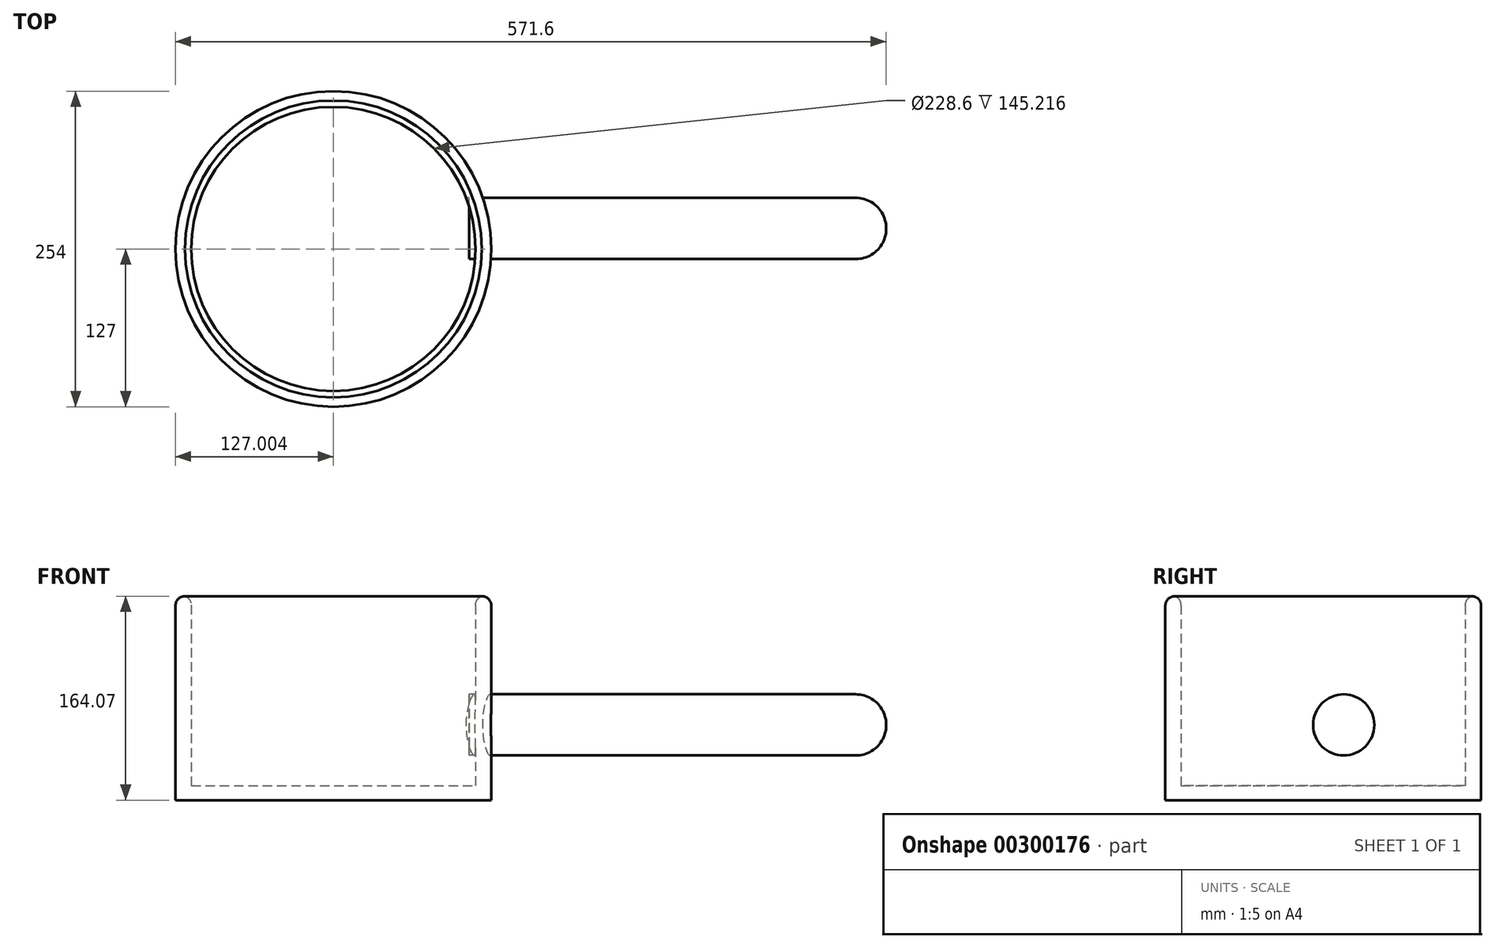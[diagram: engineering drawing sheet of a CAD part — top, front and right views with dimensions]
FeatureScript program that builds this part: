
annotation { "Feature Type Name" : "Feature", "Feature Type Description" : "" }
export const myFeature = defineFeature(function(context is Context, id is Id, definition is map)
    precondition{}
    {
        {
            var Q0;
            Q0=qCreatedBy(makeId("Front.planeOp"),FACE);
            var sketch = newSketch(context, id + "F0", { "sketchPlane" : qUnion([Q0])});
            skLineSegment(sketch, "E0", {"start": v(-61.06, 103.53) * mm, "end": v(-48.36, 103.53) * mm});
            skLineSegment(sketch, "E1", {"start": v(-48.36, 103.53) * mm, "end": v(-48.36, -48.87) * mm});
            skLineSegment(sketch, "E2", {"start": v(-48.36, -48.87) * mm, "end": v(53.24, -48.87) * mm});
            skLineSegment(sketch, "E3", {"start": v(53.24, -48.87) * mm, "end": v(53.24, 103.53) * mm});
            skLineSegment(sketch, "E4", {"start": v(53.24, 103.53) * mm, "end": v(65.94, 103.53) * mm});
            skLineSegment(sketch, "E5", {"start": v(65.94, 103.53) * mm, "end": v(65.94, -60.54) * mm});
            skLineSegment(sketch, "E6", {"start": v(65.94, -60.54) * mm, "end": v(-61.06, -60.54) * mm});
            skLineSegment(sketch, "E7", {"start": v(-61.06, -60.54) * mm, "end": v(-61.06, 103.53) * mm});
            skLineSegment(sketch, "E8", {"start": v(0, 103.85) * mm, "end": v(0, -60.54) * mm, "construction": true});
            skSolve(sketch);
        }
        {
            var Q0;
            Q0 = qSketchRegion(id + "F0", true);
            var Q1;
            Q1=sQuery(id+"F0.wireOp",EDGE,"E7");
            revolve(context, id + "F1", {"entities" : qUnion([Q0]), "axis" : qUnion([Q1]), "revolveType" : RevolveType.FULL});
        }
        {
            var Q0;
            Q0=makeQuery(id+"F1.opRevolve","SWEPT_EDGE",EDGE,{"disambiguationData":[OSD([sQuery(id+"F0.wireOp",EDGE,"E4"),sQuery(id+"F0.wireOp",EDGE,"E5")])]});
            fillet(context, id + "F2", {"entities" : qUnion([Q0]), "radius" : 7.62 * mm, "tangentPropagation" : true, "allowEdgeOverflow" : false});
        }
        {
            var Q0;
            {var subQ0=sQuery(id+"F0.wireOp",EDGE,"E4");Q0=makeQuery(id+"F2.opFillet","BLEND_EDGE",EDGE,{"blendedFrom":[makeQuery(id+"F1.opRevolve","SWEPT_EDGE",EDGE,{"disambiguationData":[OSD([subQ0,sQuery(id+"F0.wireOp",EDGE,"E5")])]}),makeQuery(id+"F1.opRevolve","SWEPT_FACE",FACE,{"disambiguationData":[OSD([subQ0])]})],"blendedInto":[makeQuery(id+"F1.opRevolve","SWEPT_FACE",FACE,{"disambiguationData":[OSD([subQ0])]})]});}
            var Q1;
            Q1=makeQuery(id+"F1.opRevolve","SWEPT_EDGE",EDGE,{"disambiguationData":[OSD([sQuery(id+"F0.wireOp",EDGE,"E3"),sQuery(id+"F0.wireOp",EDGE,"E4")])]});
            fillet(context, id + "F3", {"entities" : qUnion([Q0, Q1]), "radius" : 7.62 * mm, "tangentPropagation" : true, "allowEdgeOverflow" : false});
        }
        {
            var Q0;
            Q0=makeQuery(id+"F1.opRevolve","SWEPT_FACE",FACE,{"disambiguationData":[OSD([sQuery(id+"F0.wireOp",EDGE,"E0")])]});
            extrude(context, id + "F4", {"entities" : qUnion([Q0]), "operationType" : NewBodyOperationType.REMOVE, "oppositeDirection" : true, "depth" : 152.4 * mm});
        }
        {
            var Q0;
            Q0=qCreatedBy(makeId("Right.planeOp"),FACE);
            var sketch = newSketch(context, id + "F5", { "sketchPlane" : qUnion([Q0])});
            skCircle(sketch, "E9", {"center": v(16.45, 0) * mm, "radius": 24.6 * mm});
            skSolve(sketch);
        }
        {
            var Q0;
            Q0=makeQuery(id+"F5.imprint","IMPRINT",FACE,{"disambiguationData":[TD([[makeQuery(id+"F5.imprint","IMPRINT",EDGE,{"derivedFrom":sQuery(id+"F5.wireOp",EDGE,"E9")}),1.0]])]});
            extrude(context, id + "F6", {"entities" : qUnion([Q0]), "operationType" : NewBodyOperationType.ADD, "depth" : 383.54 * mm});
        }
        {
            var Q0;
            Q0=makeQuery(id+"F6.opExtrude","CAP_EDGE",EDGE,{"disambiguationData":[OSD([sQuery(id+"F5.wireOp",EDGE,"E9")])],"isStart":false});
            fillet(context, id + "F7", {"entities" : qUnion([Q0]), "radius" : 24.51 * mm, "tangentPropagation" : true, "allowEdgeOverflow" : false});
        }
        {
            var Q0;
            Q0=makeQuery(id+"F6.opExtrude","CAP_FACE",FACE,{"disambiguationData":[OSD([sQuery(id+"F5.wireOp",EDGE,"E9")])],"isStart":true});
            extrude(context, id + "F8", {"entities" : qUnion([Q0]), "operationType" : NewBodyOperationType.REMOVE, "oppositeDirection" : true, "depth" : 48.26 * mm});
        }
    });
